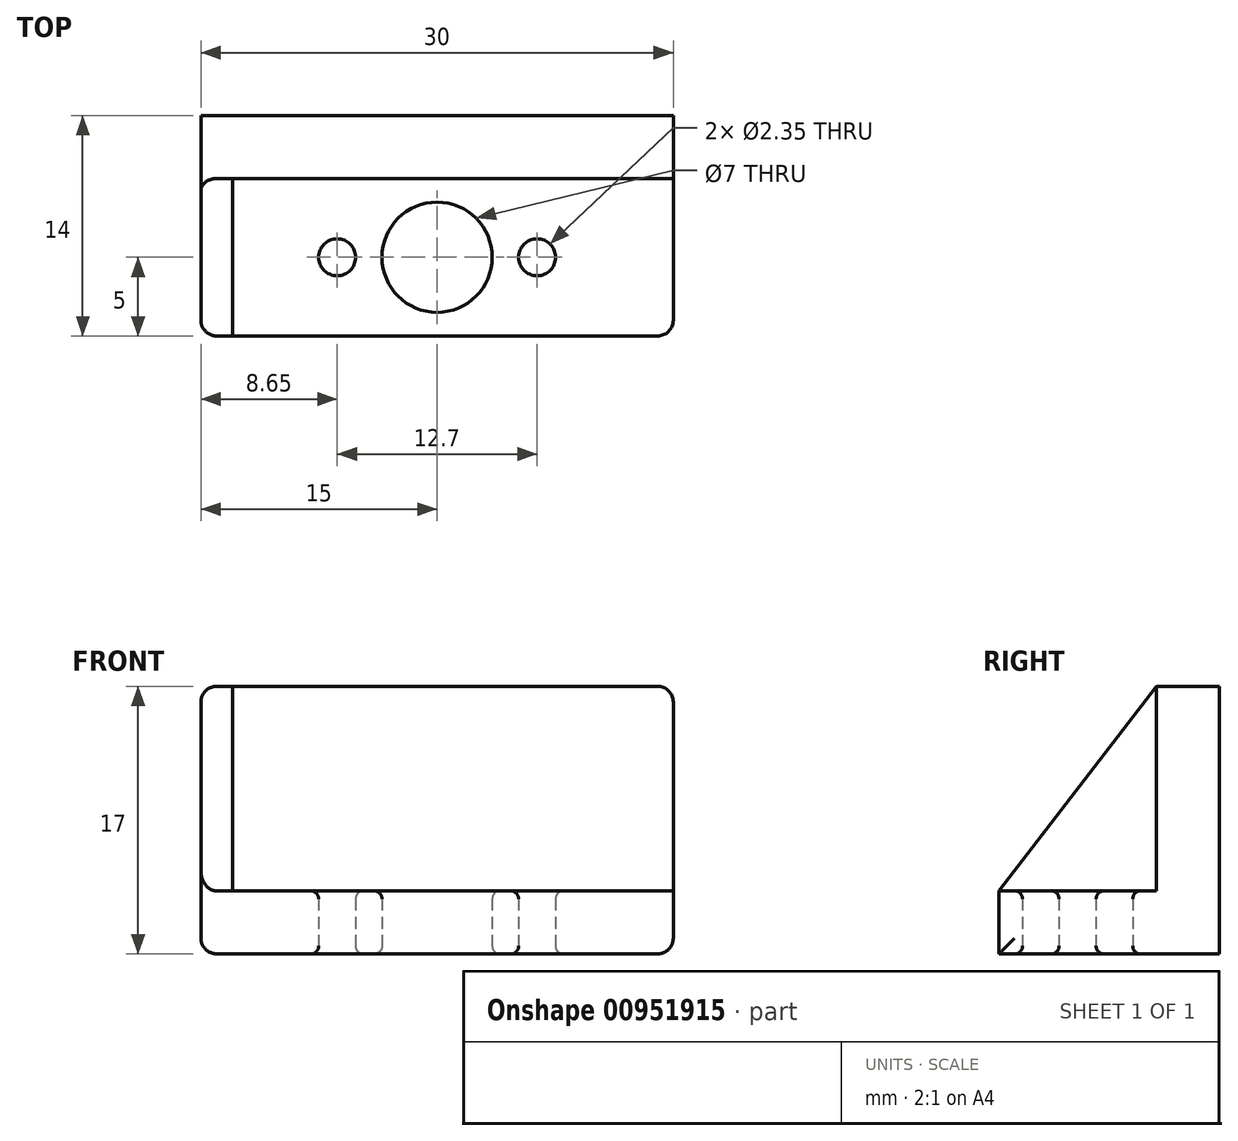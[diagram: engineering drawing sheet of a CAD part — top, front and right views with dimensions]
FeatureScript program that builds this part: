
annotation { "Feature Type Name" : "Feature", "Feature Type Description" : "" }
export const myFeature = defineFeature(function(context is Context, id is Id, definition is map)
    precondition{}
    {
        {
            var Q0;
            Q0=qCreatedBy(makeId("Top.planeOp"),FACE);
            var sketch = newSketch(context, id + "F0", { "sketchPlane" : qUnion([Q0])});
            skLineSegment(sketch, "E0.bottom", {"start": v(-15, -5) * mm, "end": v(15, -5) * mm});
            skLineSegment(sketch, "E0.top", {"start": v(-15, 5) * mm, "end": v(15, 5) * mm});
            skLineSegment(sketch, "E0.left", {"start": v(-15, -5) * mm, "end": v(-15, 5) * mm});
            skLineSegment(sketch, "E0.right", {"start": v(15, -5) * mm, "end": v(15, 5) * mm});
            skPoint(sketch, "E0.middle", {"position": v(0, 0) * mm});
            skCircle(sketch, "E1", {"center": v(0, 0) * mm, "radius": 3.5 * mm});
            skCircle(sketch, "E2", {"center": v(6.35, 0) * mm, "radius": 1.18 * mm});
            skCircle(sketch, "E3", {"center": v(-6.35, 0) * mm, "radius": 1.18 * mm});
            skLineSegment(sketch, "E4", {"start": v(-15, 5) * mm, "end": v(-15, 9) * mm});
            skLineSegment(sketch, "E5", {"start": v(-15, 9) * mm, "end": v(15, 9) * mm});
            skLineSegment(sketch, "E6", {"start": v(15, 9) * mm, "end": v(15, 5) * mm});
            skSolve(sketch);
        }
        {
            var Q0;
            Q0=makeQuery(id+"F0.imprint","IMPRINT",FACE,{"disambiguationData":[TD([[makeQuery(id+"F0.imprint","IMPRINT",EDGE,{"derivedFrom":sQuery(id+"F0.wireOp",EDGE,"E0.bottom")}),1.0]])]});
            var Q1;
            Q1=makeQuery(id+"F0.imprint","IMPRINT",FACE,{"disambiguationData":[TD([[makeQuery(id+"F0.imprint","IMPRINT",EDGE,{"derivedFrom":sQuery(id+"F0.wireOp",EDGE,"E0.top")}),1.0]])]});
            extrude(context, id + "F1", {"entities" : qUnion([Q0, Q1]), "depth" : 4 * mm, "offsetDistance" : 25 * mm});
        }
        {
            var Q0;
            Q0=makeQuery(id+"F1.opExtrude","SWEPT_FACE",FACE,{"disambiguationData":[OSD([sQuery(id+"F0.wireOp",EDGE,"E5")])]});
            var sketch = newSketch(context, id + "F2", { "sketchPlane" : qUnion([Q0])});
            skLineSegment(sketch, "E7", {"start": v(-15, 4) * mm, "end": v(-15, 17) * mm});
            skLineSegment(sketch, "E8", {"start": v(-15, 17) * mm, "end": v(15, 17) * mm});
            skLineSegment(sketch, "E9", {"start": v(15, 17) * mm, "end": v(15, 4) * mm});
            skPoint(sketch, "E10", {"position": v(-18.75, 10.5) * mm});
            skPoint(sketch, "E10.positionSnap0", {"position": v(-15, 10.5) * mm});
            skPoint(sketch, "E11", {"position": v(18.75, 10.5) * mm});
            skPoint(sketch, "E11.positionSnap0", {"position": v(15, 10.5) * mm});
            skArc(sketch, "E12", {"start": v(-18.75, 6.75) * mm, "mid": v(-22.5, 10.5) * mm, "end": v(-18.75, 14.25) * mm});
            skLineSegment(sketch, "E13", {"start": v(-18.75, 14.25) * mm, "end": v(-15, 14.25) * mm});
            skLineSegment(sketch, "E14", {"start": v(-18.75, 6.75) * mm, "end": v(-15, 6.75) * mm});
            skArc(sketch, "E15", {"start": v(18.75, 14.25) * mm, "mid": v(22.5, 10.5) * mm, "end": v(18.75, 6.75) * mm});
            skLineSegment(sketch, "E16", {"start": v(18.75, 14.25) * mm, "end": v(15, 14.25) * mm});
            skLineSegment(sketch, "E17", {"start": v(18.75, 6.75) * mm, "end": v(15, 6.75) * mm});
            skCircle(sketch, "E18", {"center": v(-18.75, 10.5) * mm, "radius": 1.75 * mm});
            skCircle(sketch, "E19", {"center": v(18.75, 10.5) * mm, "radius": 1.75 * mm});
            skSolve(sketch);
        }
        {
            var Q0;
            Q0=makeQuery(id+"F2.imprint","IMPRINT",FACE,{"disambiguationData":[TD([[makeQuery(id+"F2.imprint","IMPRINT",EDGE,{"derivedFrom":sQuery(id+"F2.wireOp",EDGE,"E7")}),-1.0]])]});
            var Q1;
            Q1=makeQuery(id+"F2.imprint","IMPRINT",FACE,{"disambiguationData":[TD([[makeQuery(id+"F2.imprint","IMPRINT",EDGE,{"derivedFrom":sQuery(id+"F2.wireOp",EDGE,"E12")}),-1.0]])]});
            var Q2;
            Q2=makeQuery(id+"F2.imprint","IMPRINT",FACE,{"disambiguationData":[TD([[makeQuery(id+"F2.imprint","IMPRINT",EDGE,{"derivedFrom":sQuery(id+"F2.wireOp",EDGE,"E15")}),-1.0]])]});
            extrude(context, id + "F3", {"entities" : qUnion([Q0, Q1, Q2]), "operationType" : NewBodyOperationType.ADD, "oppositeDirection" : true, "depth" : 4 * mm, "offsetDistance" : 25 * mm});
        }
        {
            var Q0;
            {var subQ0=sQuery(id+"F2.wireOp",EDGE,"E9");var subQ2=sQuery(id+"F0.wireOp",EDGE,"E4");Q0=makeQuery(id+"F3.boolean.opBoolean","MERGE",FACE,{"derivedFrom":[makeQuery(id+"F1.opExtrude","SWEPT_FACE",FACE,{"disambiguationData":[OSD([sQuery(id+"F0.wireOp",EDGE,"E0.left"),subQ2])]}),makeQuery(id+"F3.opExtrude","SWEPT_FACE",FACE,{"disambiguationData":[OSD([subQ0]),TDD([makeQuery(id+"F2.imprint","IMPRINT",EDGE,{"disambiguationData":[TD([[makeQuery(id+"F2.imprint","INTERSECT",VERTEX,{"derivedFrom":[subQ0,sQuery(id+"F2.wireOp",EDGE,"E17")]}),-1.0]])],"derivedFrom":subQ0})])]})]});}
            var sketch = newSketch(context, id + "F4", { "sketchPlane" : qUnion([Q0])});
            skLineSegment(sketch, "E20.0.0", {"start": v(-9, 17) * mm, "end": v(-9, 14.25) * mm});
            skLineSegment(sketch, "E20.0.1", {"start": v(-9, 14.25) * mm, "end": v(-5, 14.25) * mm});
            skLineSegment(sketch, "E20.0.2", {"start": v(-5, 14.25) * mm, "end": v(-5, 17) * mm});
            skLineSegment(sketch, "E20.0.3", {"start": v(-5, 17) * mm, "end": v(-9, 17) * mm});
            skLineSegment(sketch, "E21", {"start": v(-5, 17) * mm, "end": v(5, 4) * mm});
            skLineSegment(sketch, "E22", {"start": v(5, 4) * mm, "end": v(-5, 4) * mm});
            skLineSegment(sketch, "E23", {"start": v(-5, 4) * mm, "end": v(-5, 17) * mm});
            skSolve(sketch);
        }
        {
            var Q0;
            {var subQ4=sQuery(id+"F4.wireOp",EDGE,"E21");Q0=makeQuery(id+"F4.imprint","IMPRINT",FACE,{"disambiguationData":[TD([[makeQuery(id+"F4.imprint","IMPRINT",EDGE,{"derivedFrom":subQ4}),-1.0]])]});}
            extrude(context, id + "F5", {"entities" : qUnion([Q0]), "operationType" : NewBodyOperationType.ADD, "oppositeDirection" : true, "depth" : 2 * mm, "offsetDistance" : 25 * mm});
        }
        {
            var Q0;
            {var subQ0=sQuery(id+"F2.wireOp",EDGE,"E7");var subQ2=sQuery(id+"F0.wireOp",EDGE,"E6");Q0=makeQuery(id+"F3.boolean.opBoolean","MERGE",FACE,{"derivedFrom":[makeQuery(id+"F1.opExtrude","SWEPT_FACE",FACE,{"disambiguationData":[OSD([sQuery(id+"F0.wireOp",EDGE,"E0.right"),subQ2])]}),makeQuery(id+"F3.opExtrude","SWEPT_FACE",FACE,{"disambiguationData":[OSD([subQ0]),TDD([makeQuery(id+"F2.imprint","IMPRINT",EDGE,{"disambiguationData":[TD([[makeQuery(id+"F2.imprint","INTERSECT",VERTEX,{"derivedFrom":[subQ0,sQuery(id+"F2.wireOp",EDGE,"E14")]}),1.0]])],"derivedFrom":subQ0})])]})]});}
            var sketch = newSketch(context, id + "F6", { "sketchPlane" : qUnion([Q0])});
            skLineSegment(sketch, "E24.0.0", {"start": v(9, 14.25) * mm, "end": v(9, 17) * mm});
            skLineSegment(sketch, "E24.0.1", {"start": v(9, 17) * mm, "end": v(5, 17) * mm});
            skLineSegment(sketch, "E24.0.2", {"start": v(5, 17) * mm, "end": v(5, 14.25) * mm});
            skLineSegment(sketch, "E24.0.3", {"start": v(5, 14.25) * mm, "end": v(9, 14.25) * mm});
            skLineSegment(sketch, "E25", {"start": v(-5, 4) * mm, "end": v(5, 17) * mm});
            skLineSegment(sketch, "E26", {"start": v(5, 4) * mm, "end": v(-5, 4) * mm});
            skLineSegment(sketch, "E27", {"start": v(5, 14.25) * mm, "end": v(5, 4) * mm});
            skSolve(sketch);
        }
        {
            var Q0;
            {var subQ3=sQuery(id+"F6.wireOp",EDGE,"E24.0.2");Q0=makeQuery(id+"F6.imprint","IMPRINT",FACE,{"disambiguationData":[TD([[makeQuery(id+"F6.imprint","IMPRINT",EDGE,{"derivedFrom":subQ3}),-1.0]])]});}
            extrude(context, id + "F7", {"entities" : qUnion([Q0]), "operationType" : NewBodyOperationType.ADD, "oppositeDirection" : true, "depth" : 2 * mm, "offsetDistance" : 25 * mm});
        }
        {
            var Q0;
            Q0=makeQuery(id+"F7.opExtrude","CAP_EDGE",EDGE,{"disambiguationData":[OSD([sQuery(id+"F6.wireOp",EDGE,"E24.0.2"),sQuery(id+"F6.wireOp",EDGE,"E27")])],"isStart":false});
            var Q1;
            Q1=makeQuery(id+"F5.opExtrude","CAP_EDGE",EDGE,{"disambiguationData":[OSD([sQuery(id+"F4.wireOp",EDGE,"E23")])],"isStart":false});
            var Q2;
            Q2=makeQuery(id+"F5.opExtrude","CAP_EDGE",EDGE,{"disambiguationData":[OSD([sQuery(id+"F4.wireOp",EDGE,"E22")])],"isStart":false});
            var Q3;
            Q3=makeQuery(id+"F7.opExtrude","CAP_EDGE",EDGE,{"disambiguationData":[OSD([sQuery(id+"F6.wireOp",EDGE,"E26")])],"isStart":false});
            var Q4;
            Q4=makeQuery(id+"F3.opExtrude","SWEPT_EDGE",EDGE,{"disambiguationData":[OSD([sQuery(id+"F2.wireOp",EDGE,"E7"),sQuery(id+"F2.wireOp",EDGE,"E13")])]});
            var Q5;
            Q5=makeQuery(id+"F3.opExtrude","SWEPT_EDGE",EDGE,{"disambiguationData":[OSD([sQuery(id+"F2.wireOp",EDGE,"E7"),sQuery(id+"F2.wireOp",EDGE,"E14")])]});
            var Q6;
            Q6=makeQuery(id+"F3.opExtrude","SWEPT_EDGE",EDGE,{"disambiguationData":[OSD([sQuery(id+"F2.wireOp",EDGE,"E9"),sQuery(id+"F2.wireOp",EDGE,"E17")])]});
            var Q7;
            Q7=makeQuery(id+"F3.opExtrude","SWEPT_EDGE",EDGE,{"disambiguationData":[OSD([sQuery(id+"F2.wireOp",EDGE,"E9"),sQuery(id+"F2.wireOp",EDGE,"E16")])]});
            var Q8;
            Q8=makeQuery(id+"F5.opExtrude","CAP_EDGE",EDGE,{"disambiguationData":[OSD([sQuery(id+"F4.wireOp",EDGE,"E23")])],"isStart":true});
            var Q9;
            Q9=makeQuery(id+"F7.opExtrude","CAP_EDGE",EDGE,{"disambiguationData":[OSD([sQuery(id+"F6.wireOp",EDGE,"E24.0.2"),sQuery(id+"F6.wireOp",EDGE,"E27")])],"isStart":true});
            var Q10;
            Q10=makeQuery(id+"F1.opExtrude","SWEPT_EDGE",EDGE,{"disambiguationData":[OSD([sQuery(id+"F0.wireOp",EDGE,"E0.bottom"),sQuery(id+"F0.wireOp",EDGE,"E0.right")])]});
            var Q11;
            Q11=makeQuery(id+"F1.opExtrude","SWEPT_EDGE",EDGE,{"disambiguationData":[OSD([sQuery(id+"F0.wireOp",EDGE,"E0.bottom"),sQuery(id+"F0.wireOp",EDGE,"E0.left")])]});
            var Q12;
            Q12=makeQuery(id+"F3.opExtrude","SWEPT_EDGE",EDGE,{"disambiguationData":[OSD([sQuery(id+"F2.wireOp",EDGE,"E7"),sQuery(id+"F2.wireOp",EDGE,"E8")])]});
            var Q13;
            Q13=makeQuery(id+"F1.opExtrude","CAP_EDGE",EDGE,{"disambiguationData":[OSD([sQuery(id+"F0.wireOp",EDGE,"E0.right"),sQuery(id+"F0.wireOp",EDGE,"E6")])],"isStart":true});
            var Q14;
            Q14=makeQuery(id+"F3.opExtrude","SWEPT_EDGE",EDGE,{"disambiguationData":[OSD([sQuery(id+"F2.wireOp",EDGE,"E8"),sQuery(id+"F2.wireOp",EDGE,"E9")])]});
            var Q15;
            Q15=makeQuery(id+"F1.opExtrude","CAP_EDGE",EDGE,{"disambiguationData":[OSD([sQuery(id+"F0.wireOp",EDGE,"E0.left"),sQuery(id+"F0.wireOp",EDGE,"E4")])],"isStart":true});
            fillet(context, id + "F8", {"entities" : qUnion([Q0, Q1, Q2, Q3, Q4, Q5, Q6, Q7, Q8, Q9, Q10, Q11, Q12, Q13, Q14, Q15]), "radius" : 1 * mm, "tangentPropagation" : true, "allowEdgeOverflow" : false});
        }
        {
            var Q0;
            Q0=makeQuery(id+"F1.opExtrude","SWEPT_FACE",FACE,{"disambiguationData":[OSD([sQuery(id+"F0.wireOp",EDGE,"E2")])]});
            var Q1;
            Q1=makeQuery(id+"F1.opExtrude","SWEPT_FACE",FACE,{"disambiguationData":[OSD([sQuery(id+"F0.wireOp",EDGE,"E3")])]});
            var Q2;
            Q2=makeQuery(id+"F1.opExtrude","SWEPT_FACE",FACE,{"disambiguationData":[OSD([sQuery(id+"F0.wireOp",EDGE,"E1")])]});
            fillet(context, id + "F9", {"entities" : qUnion([Q0, Q1, Q2]), "radius" : .5 * mm, "tangentPropagation" : true, "allowEdgeOverflow" : false});
        }
    });
